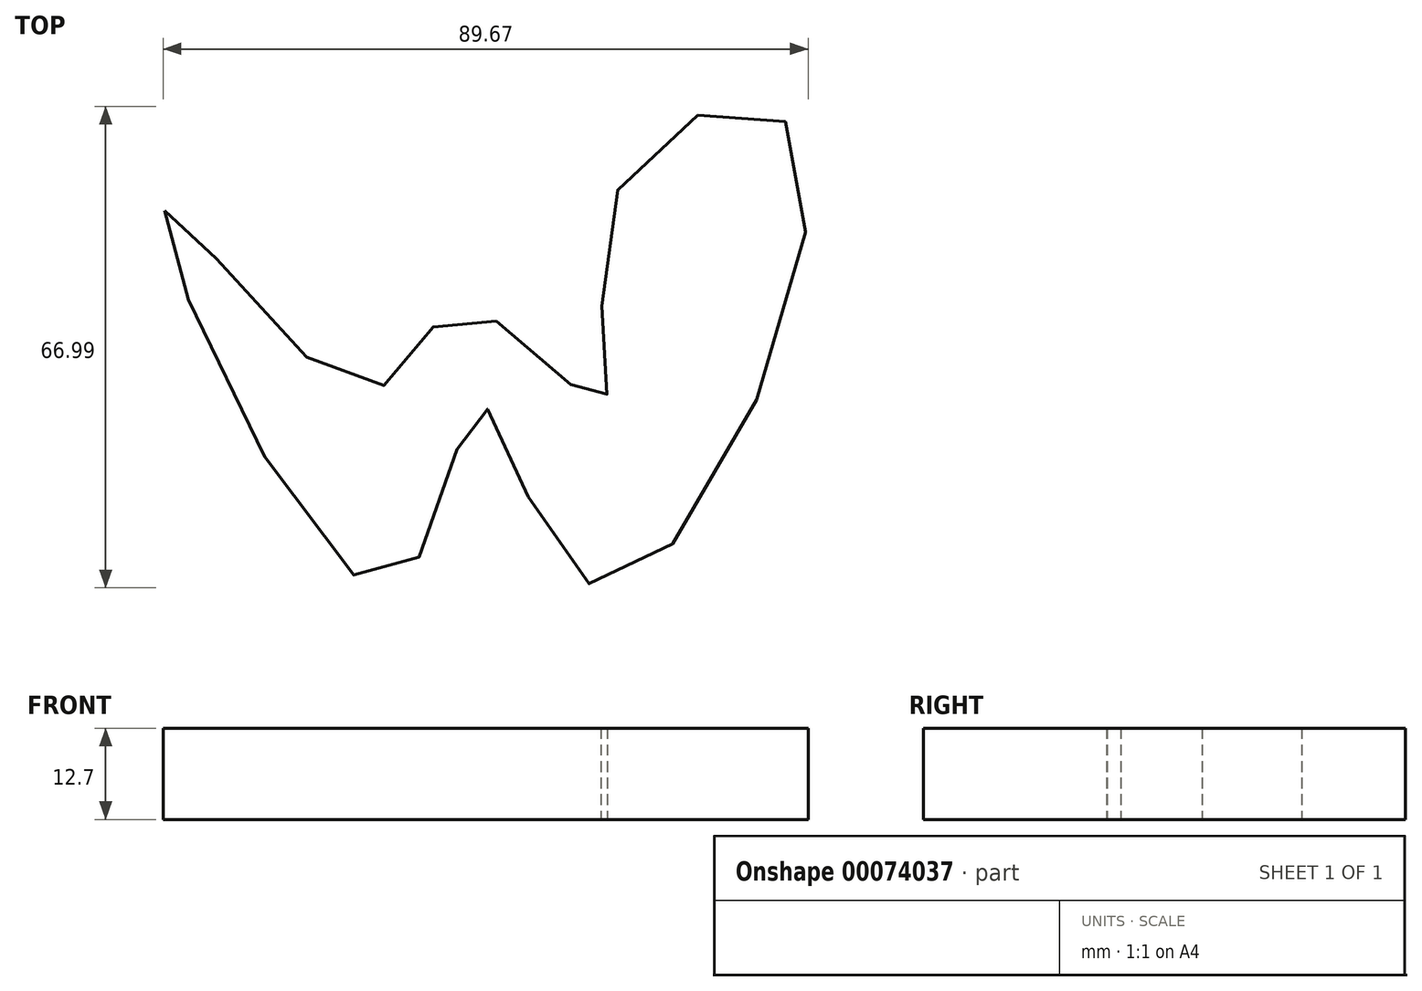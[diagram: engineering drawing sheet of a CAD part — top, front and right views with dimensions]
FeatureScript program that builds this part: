
annotation { "Feature Type Name" : "Feature", "Feature Type Description" : "" }
export const myFeature = defineFeature(function(context is Context, id is Id, definition is map)
    precondition{}
    {
        {
            var Q0;
            Q0=qCreatedBy(makeId("Top.planeOp"),FACE);
            var sketch = newSketch(context, id + "F1", { "sketchPlane" : qUnion([Q0])});
            skFitSpline(sketch, "E0", {"points": [v(-12.18, 52.4) * mm, v(18.43, 0) * mm, v(31.54, 25.42) * mm, v(48.4, 0) * mm, v(75.9, 62.43) * mm, v(50.9, 55.52) * mm, v(48.4, 25.51) * mm, v(29.05, 38.64) * mm, v(15.3, 27.4) * mm, v(-12.18, 52.4) * mm]});
            skSolve(sketch);
        }
        {
            var Q0;
            Q0=makeQuery(id+"F1.imprint","IMPRINT",FACE,{"disambiguationData":[TD([[makeQuery(id+"F1.imprint","IMPRINT",EDGE,{"derivedFrom":sQuery(id+"F1.wireOp",EDGE,"E0")}),1.0]])]});
            extrude(context, id + "F0", {"entities" : qUnion([Q0]), "depth" : 12.7 * mm});
        }
    });
